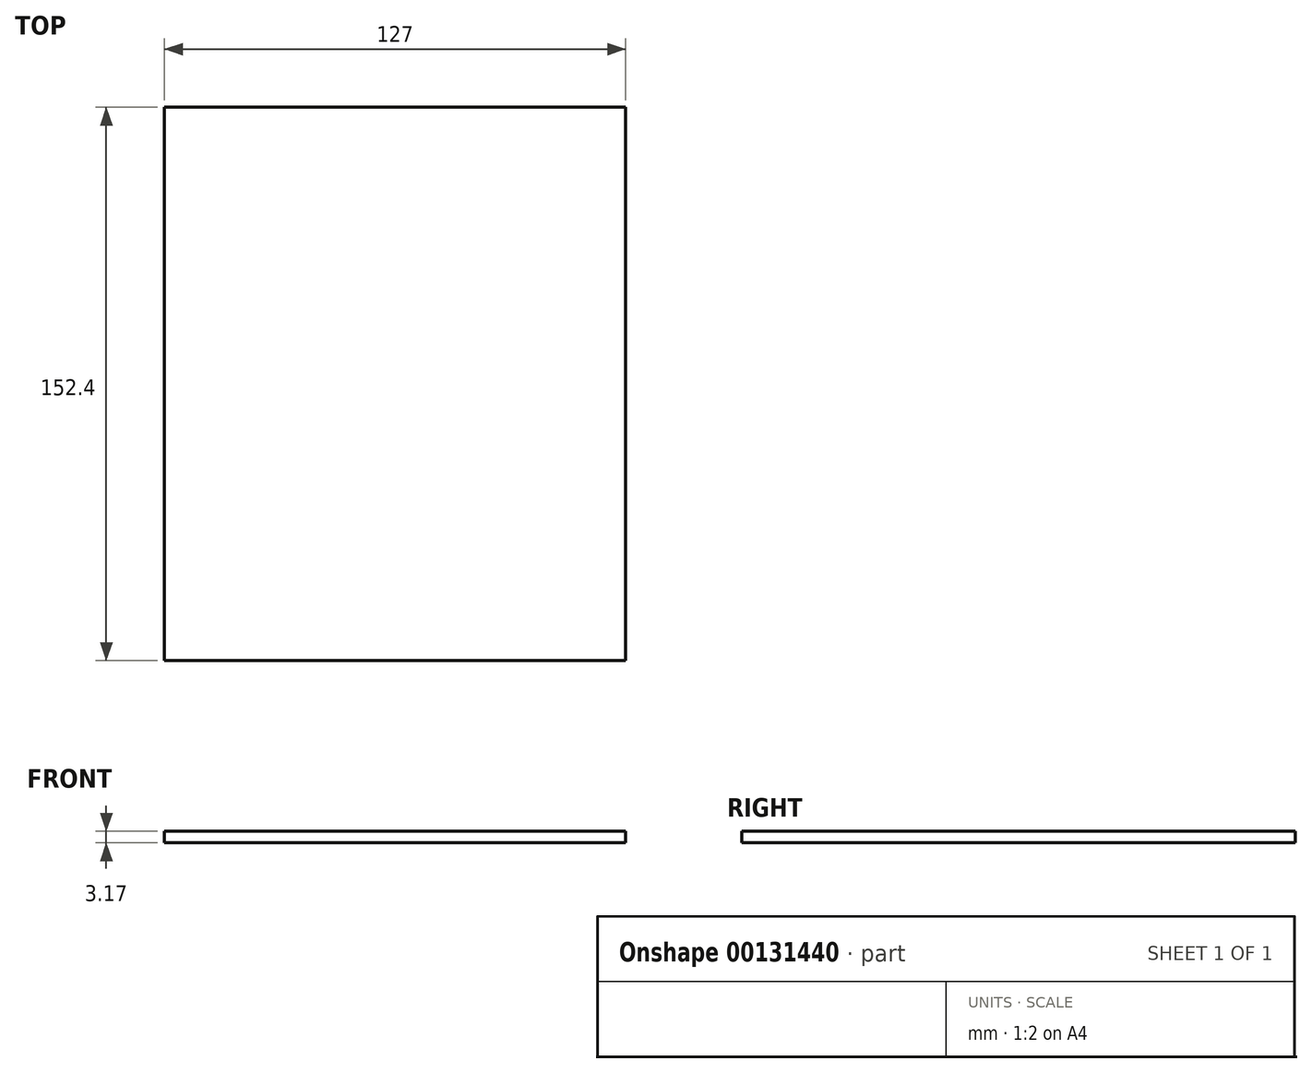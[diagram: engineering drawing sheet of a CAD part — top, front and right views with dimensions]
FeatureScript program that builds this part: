
annotation { "Feature Type Name" : "Feature", "Feature Type Description" : "" }
export const myFeature = defineFeature(function(context is Context, id is Id, definition is map)
    precondition{}
    {
        {
            var Q0;
            Q0=qCreatedBy(makeId("Top.planeOp"),FACE);
            var sketch = newSketch(context, id + "F0", { "sketchPlane" : qUnion([Q0])});
            skLineSegment(sketch, "E0.bottom", {"start": v(-70.2, 106.53) * mm, "end": v(56.8, 106.53) * mm});
            skLineSegment(sketch, "E0.top", {"start": v(-70.2, -45.87) * mm, "end": v(56.8, -45.87) * mm});
            skLineSegment(sketch, "E0.left", {"start": v(-70.2, 106.53) * mm, "end": v(-70.2, -45.87) * mm});
            skLineSegment(sketch, "E0.right", {"start": v(56.8, 106.53) * mm, "end": v(56.8, -45.87) * mm});
            skSolve(sketch);
        }
        {
            var Q0;
            Q0 = qSketchRegion(id + "F0", true);
            extrude(context, id + "F1", {"entities" : qUnion([Q0]), "depth" : 3.17 * mm});
        }
    });
